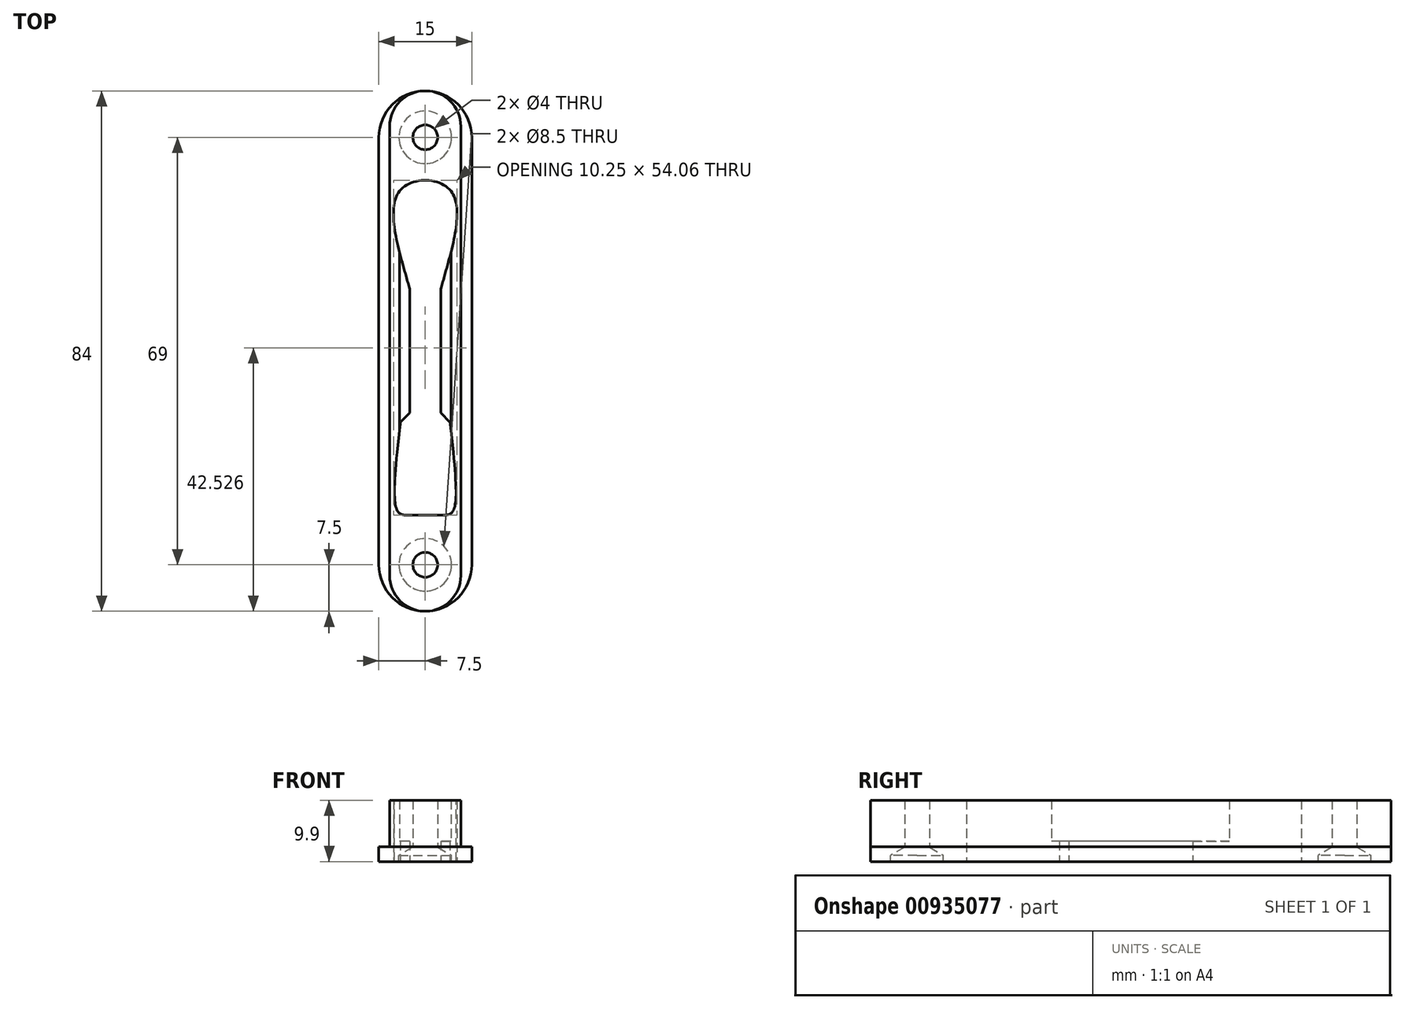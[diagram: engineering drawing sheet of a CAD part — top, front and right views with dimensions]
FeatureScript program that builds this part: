
annotation { "Feature Type Name" : "Feature", "Feature Type Description" : "" }
export const myFeature = defineFeature(function(context is Context, id is Id, definition is map)
    precondition{}
    {
        {
            var Q0;
            Q0=qCreatedBy(makeId("Top.planeOp"),FACE);
            var sketch = newSketch(context, id + "F0", { "sketchPlane" : qUnion([Q0])});
            skLineSegment(sketch, "E0", {"start": v(-7.5, 34.5) * mm, "end": v(-7.5, -34.5) * mm});
            skLineSegment(sketch, "E1", {"start": v(7.5, 34.5) * mm, "end": v(7.5, -34.5) * mm});
            skArc(sketch, "E2", {"start": v(7.5, 34.5) * mm, "mid": v(0, 42) * mm, "end": v(-7.5, 34.5) * mm});
            skArc(sketch, "E3", {"start": v(-7.5, -34.5) * mm, "mid": v(0, -42) * mm, "end": v(7.5, -34.5) * mm});
            skLineSegment(sketch, "E4", {"start": v(-2.5, 10) * mm, "end": v(-2.5, -10) * mm});
            skLineSegment(sketch, "E5", {"start": v(2.5, 10) * mm, "end": v(2.5, -10) * mm});
            skLineSegment(sketch, "E6", {"start": v(2.5, -10) * mm, "end": v(4, -11.5) * mm});
            skLineSegment(sketch, "E7", {"start": v(-2.5, -10) * mm, "end": v(-4, -11.5) * mm});
            skFitSpline(sketch, "E8", {"points": [v(-2.5, 10) * mm, v(-4, 26) * mm, v(4, 26) * mm, v(2.5, 10) * mm], "startDerivative": vector(-13.4, 48.21) * mm, "endDerivative": vector(-13.4, -48.21) * mm});
            skFitSpline(sketch, "E9", {"points": [v(-4, -11.5) * mm, v(-2.5, -26.5) * mm, v(2.5, -26.5) * mm, v(4, -11.5) * mm], "startDerivative": vector(-13.52, -115.53) * mm, "endDerivative": vector(-13.52, 115.53) * mm});
            skLineSegment(sketch, "E10", {"start": v(-2.5, 10) * mm, "end": v(2.5, -10) * mm, "construction": true});
            skLineSegment(sketch, "E11", {"start": v(7.5, 34.5) * mm, "end": v(-7.5, -34.5) * mm, "construction": true});
            skCircle(sketch, "E12", {"center": v(0, 34.5) * mm, "radius": 2 * mm});
            skCircle(sketch, "E13", {"center": v(0, -34.5) * mm, "radius": 2 * mm});
            skLineSegment(sketch, "E14", {"start": v(-5.75, 36.25) * mm, "end": v(-5.75, -36.25) * mm});
            skLineSegment(sketch, "E15", {"start": v(5.75, 36.25) * mm, "end": v(5.75, -36.25) * mm});
            skArc(sketch, "E16", {"start": v(5.75, 36.25) * mm, "mid": v(0, 42) * mm, "end": v(-5.75, 36.25) * mm});
            skArc(sketch, "E17", {"start": v(-5.75, -36.25) * mm, "mid": v(0, -42) * mm, "end": v(5.75, -36.25) * mm});
            skLineSegment(sketch, "E18.bottom", {"start": v(-4.15, 27.56) * mm, "end": v(4.15, 27.56) * mm});
            skLineSegment(sketch, "E18.top", {"start": v(-4.15, -26.5) * mm, "end": v(4.15, -26.5) * mm});
            skLineSegment(sketch, "E18.left", {"start": v(-4.15, 27.56) * mm, "end": v(-4.15, -26.5) * mm});
            skLineSegment(sketch, "E18.right", {"start": v(4.15, 27.56) * mm, "end": v(4.15, -26.5) * mm});
            skLineSegment(sketch, "E19", {"start": v(5.75, -26.5) * mm, "end": v(4.15, -26.5) * mm, "construction": true});
            skLineSegment(sketch, "E20", {"start": v(-5.75, -26.5) * mm, "end": v(-4.15, -26.5) * mm, "construction": true});
            skSolve(sketch);
        }
        {
            var Q0;
            Q0=makeQuery(id+"F0.imprint","IMPRINT",FACE,{"disambiguationData":[TD([[makeQuery(id+"F0.imprint","IMPRINT",EDGE,{"derivedFrom":sQuery(id+"F0.wireOp",EDGE,"E12")}),-1.0]])]});
            var Q1;
            {var subQ0=sQuery(id+"F0.wireOp",EDGE,"E18.bottom");var subQ1=sQuery(id+"F0.wireOp",EDGE,"E8");var subQ2=makeQuery(id+"F0.imprint","INTERSECT",VERTEX,{"derivedFrom":[subQ1,subQ0]});Q1=makeQuery(id+"F0.imprint","IMPRINT",FACE,{"disambiguationData":[TD([[makeQuery(id+"F0.imprint","IMPRINT",EDGE,{"disambiguationData":[TD([[subQ2,-1.0]])],"derivedFrom":subQ1}),1.0]])]});}
            var Q2;
            {var subQ0=sQuery(id+"F0.wireOp",EDGE,"E18.left");var subQ1=sQuery(id+"F0.wireOp",EDGE,"E8");var subQ2=makeQuery(id+"F0.imprint","INTERSECT",VERTEX,{"disambiguationData":[OD(1.0)],"derivedFrom":[subQ1,subQ0]});Q2=makeQuery(id+"F0.imprint","IMPRINT",FACE,{"disambiguationData":[TD([[makeQuery(id+"F0.imprint","IMPRINT",EDGE,{"disambiguationData":[TD([[subQ2,-1.0]])],"derivedFrom":subQ1}),1.0]])]});}
            var Q3;
            {var subQ0=sQuery(id+"F0.wireOp",EDGE,"E18.top");var subQ1=sQuery(id+"F0.wireOp",EDGE,"E9");var subQ2=makeQuery(id+"F0.imprint","INTERSECT",VERTEX,{"derivedFrom":[subQ1,subQ0]});Q3=makeQuery(id+"F0.imprint","IMPRINT",FACE,{"disambiguationData":[TD([[makeQuery(id+"F0.imprint","IMPRINT",EDGE,{"disambiguationData":[TD([[subQ2,-1.0]])],"derivedFrom":subQ1}),-1.0]])]});}
            var Q4;
            {var subQ0=sQuery(id+"F0.wireOp",EDGE,"E18.left");var subQ1=sQuery(id+"F0.wireOp",EDGE,"E9");var subQ2=makeQuery(id+"F0.imprint","INTERSECT",VERTEX,{"disambiguationData":[OD(1.0)],"derivedFrom":[subQ1,subQ0]});Q4=makeQuery(id+"F0.imprint","IMPRINT",FACE,{"disambiguationData":[TD([[makeQuery(id+"F0.imprint","IMPRINT",EDGE,{"disambiguationData":[TD([[subQ2,-1.0]])],"derivedFrom":subQ1}),-1.0]])]});}
            extrude(context, id + "F1", {"entities" : qUnion([Q0, Q1, Q2, Q3, Q4]), "depth" : 9.9 * mm, "offsetDistance" : 25 * mm});
        }
        {
            var Q0;
            {var subQ2=sQuery(id+"F0.wireOp",EDGE,"E1");Q0=makeQuery(id+"F0.imprint","IMPRINT",FACE,{"disambiguationData":[TD([[makeQuery(id+"F0.imprint","IMPRINT",EDGE,{"derivedFrom":subQ2}),-1.0]])]});}
            var Q1;
            {var subQ2=sQuery(id+"F0.wireOp",EDGE,"E0");Q1=makeQuery(id+"F0.imprint","IMPRINT",FACE,{"disambiguationData":[TD([[makeQuery(id+"F0.imprint","IMPRINT",EDGE,{"derivedFrom":subQ2}),1.0]])]});}
            extrude(context, id + "F2", {"entities" : qUnion([Q0, Q1]), "operationType" : NewBodyOperationType.ADD, "depth" : 2.4 * mm, "offsetDistance" : 25 * mm});
        }
        {
            var Q0;
            {var subQ5=sQuery(id+"F0.wireOp",EDGE,"E5");Q0=makeQuery(id+"F0.imprint","IMPRINT",FACE,{"disambiguationData":[TD([[makeQuery(id+"F0.imprint","IMPRINT",EDGE,{"derivedFrom":subQ5}),1.0]])]});}
            var Q1;
            {var subQ1=sQuery(id+"F0.wireOp",EDGE,"E4");Q1=makeQuery(id+"F0.imprint","IMPRINT",FACE,{"disambiguationData":[TD([[makeQuery(id+"F0.imprint","IMPRINT",EDGE,{"derivedFrom":subQ1}),-1.0]])]});}
            extrude(context, id + "F3", {"entities" : qUnion([Q0, Q1]), "operationType" : NewBodyOperationType.ADD, "depth" : 3.3 * mm, "offsetDistance" : 25 * mm});
        }
        {
            var Q0;
            Q0=sQuery(id+"F0.wireOp",VERTEX,"E2.center");
            var Q1;
            Q1=sQuery(id+"F0.wireOp",VERTEX,"E3.center");
            var Q2;
            Q2=makeQuery(id+"F1.opExtrude","SWEPT_BODY",BODY,{"disambiguationData":[OSD([sQuery(id+"F0.wireOp",EDGE,"E8"),sQuery(id+"F0.wireOp",EDGE,"E9"),sQuery(id+"F0.wireOp",EDGE,"E12"),sQuery(id+"F0.wireOp",EDGE,"E13"),sQuery(id+"F0.wireOp",EDGE,"E14"),sQuery(id+"F0.wireOp",EDGE,"E15"),sQuery(id+"F0.wireOp",EDGE,"E16"),sQuery(id+"F0.wireOp",EDGE,"E17"),sQuery(id+"F0.wireOp",EDGE,"E18.left"),sQuery(id+"F0.wireOp",EDGE,"E18.right")])]});
            hole(context, id + "F4", {"style" : HoleStyle.SIMPLE, "endStyle" : HoleEndStyle.BLIND, "oppositeDirection" : true, "holeDiameter" : 8.5 * mm, "majorDiameter" : 5 * mm, "holeDepth" : 1 * mm, "isTappedThrough" : true, "tappedDepth" : 12 * mm, "tapClearance" : 3, "locations" : qUnion([Q0, Q1]), "scope" : qUnion([Q2]), "startStyle" : HoleStartStyle.PART});
        }
    });
